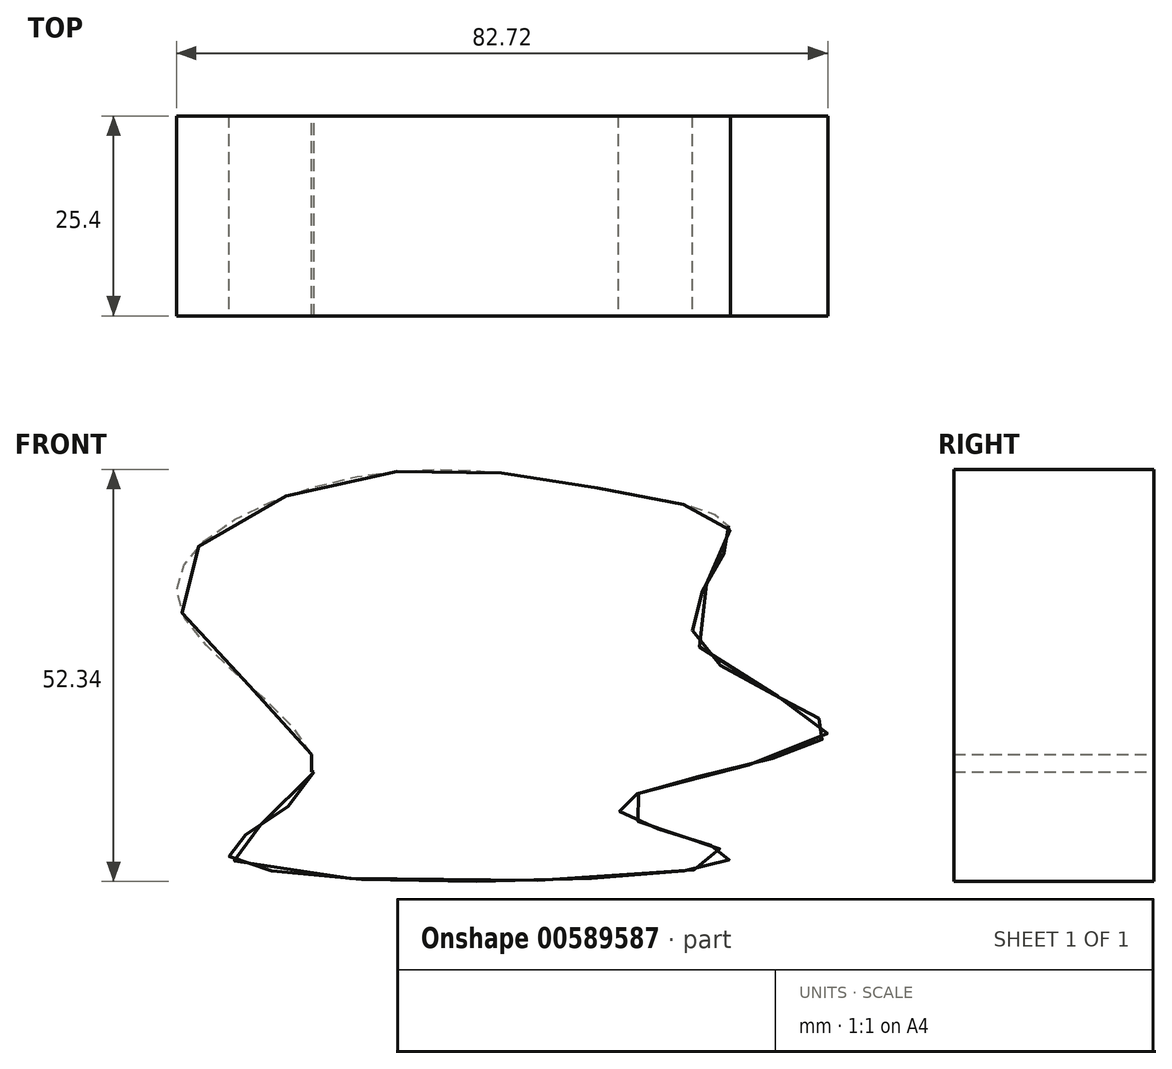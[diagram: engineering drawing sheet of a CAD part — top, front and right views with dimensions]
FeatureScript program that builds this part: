
annotation { "Feature Type Name" : "Feature", "Feature Type Description" : "" }
export const myFeature = defineFeature(function(context is Context, id is Id, definition is map)
    precondition{}
    {
        {
            var Q0;
            Q0=qCreatedBy(makeId("Front.planeOp"),FACE);
            var sketch = newSketch(context, id + "F0", { "sketchPlane" : qUnion([Q0])});
            skLineSegment(sketch, "E0.bottom", {"start": v(-53.21, 10.87) * mm, "end": v(-12.77, 10.87) * mm});
            skLineSegment(sketch, "E0.top", {"start": v(-53.21, 45.76) * mm, "end": v(-12.77, 45.76) * mm});
            skLineSegment(sketch, "E0.left", {"start": v(-53.21, 10.87) * mm, "end": v(-53.21, 45.76) * mm});
            skLineSegment(sketch, "E0.right", {"start": v(-12.77, 10.87) * mm, "end": v(-12.77, 45.76) * mm});
            skCircle(sketch, "E1", {"center": v(13.52, 22.67) * mm, "radius": 26.4 * mm});
            skPoint(sketch, "E1.first.point", {"position": v(14.79, 49.04) * mm});
            skPoint(sketch, "E1.second.point", {"position": v(37.54, 33.62) * mm});
            skPoint(sketch, "E1.third.point", {"position": v(0, 0) * mm});
            skSolve(sketch);
        }
        {
            var Q0;
            {var subQ1=sQuery(id+"F0.wireOp",EDGE,"E0.bottom");Q0=makeQuery(id+"F0.imprint","IMPRINT",FACE,{"disambiguationData":[TD([[makeQuery(id+"F0.imprint","IMPRINT",EDGE,{"derivedFrom":subQ1}),1.0]])]});}
            extrude(context, id + "F1", {"entities" : qUnion([Q0]), "depth" : 25.4 * mm, "offsetDistance" : 25.4 * mm});
        }
        {
            var Q0;
            Q0=qCreatedBy(makeId("Front.planeOp"),FACE);
            var sketch = newSketch(context, id + "F2", { "sketchPlane" : qUnion([Q0])});
            skFitSpline(sketch, "E2", {"points": [v(-12, 46) * mm, v(0, 40.95) * mm, v(-4.42, 27.55) * mm, v(12.26, 15.67) * mm, v(-14.28, 6.32) * mm, v(0, 0) * mm, v(-63.58, 0) * mm, v(-52.96, 10.36) * mm, v(-70.15, 32.36) * mm, v(-47.9, 48.28) * mm, v(-12, 46) * mm]});
            skSolve(sketch);
        }
        {
            var Q0;
            Q0=makeQuery(id+"F2.imprint","IMPRINT",FACE,{"disambiguationData":[TD([[makeQuery(id+"F2.imprint","IMPRINT",EDGE,{"derivedFrom":sQuery(id+"F2.wireOp",EDGE,"E2")}),-1.0]])]});
            extrude(context, id + "F3", {"entities" : qUnion([Q0]), "operationType" : NewBodyOperationType.ADD, "depth" : 25.4 * mm, "offsetDistance" : 25.4 * mm});
        }
    });
